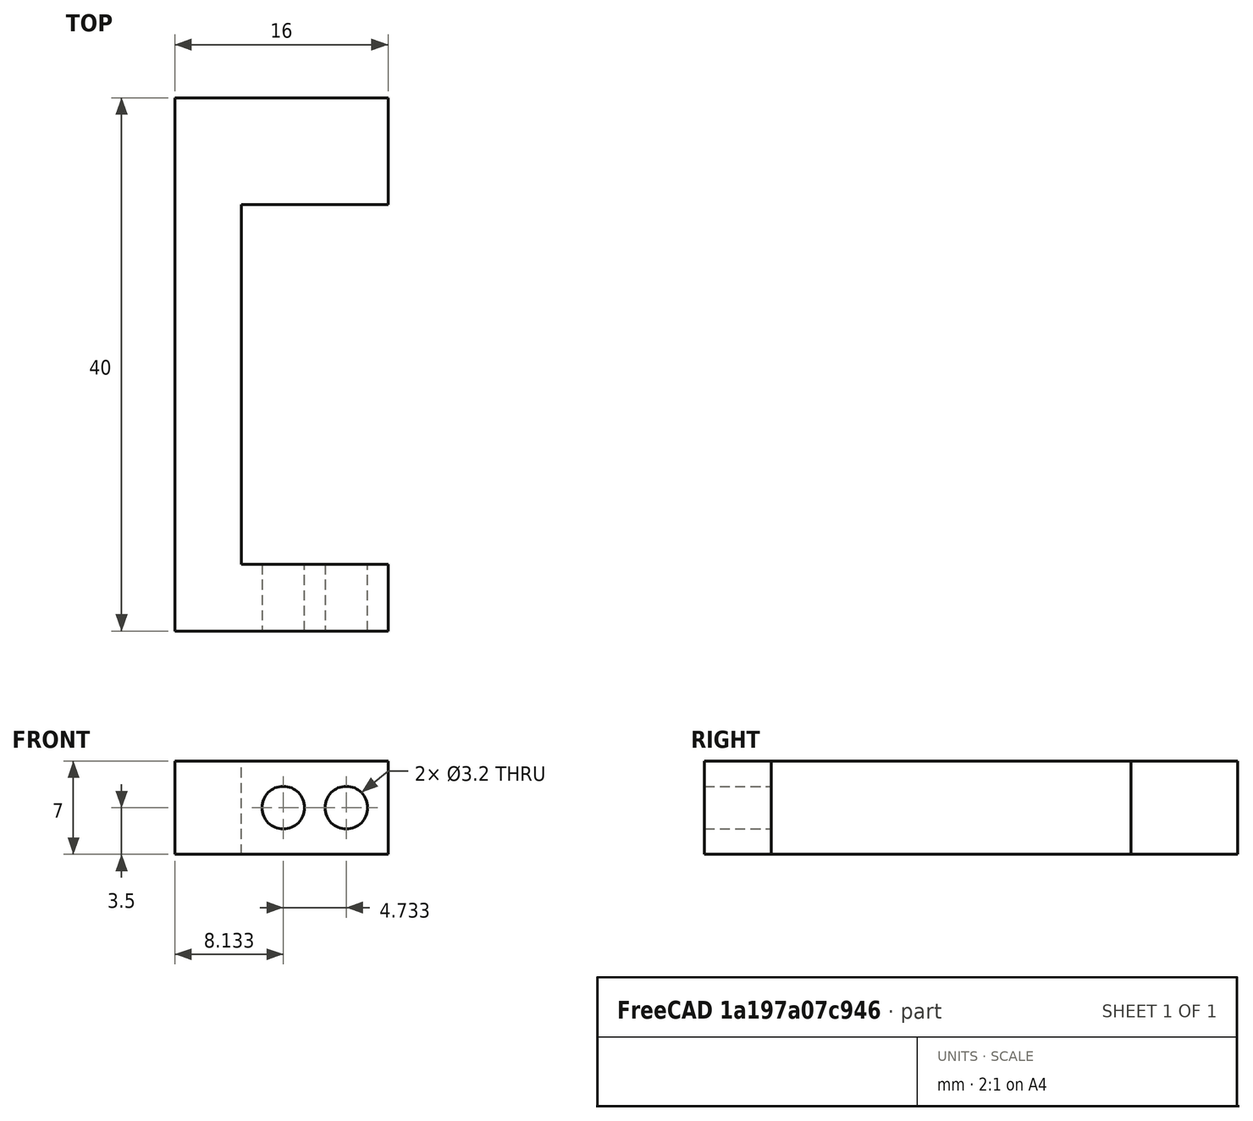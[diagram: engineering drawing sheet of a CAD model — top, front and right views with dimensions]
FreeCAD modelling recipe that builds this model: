
FCSTD DOCUMENT  (FreeCAD 0.18.4R)
Label: 10
License: All rights reserved
LicenseURL: http://en.wikipedia.org/wiki/All_rights_reserved
objects: Sketcher::SketchObject×2, PartDesign::Pad×1, PartDesign::Pocket×1, PartDesign::Body×1
note: 7 computed .brp shape members not serialized (recipe doc carries the construction recipe); baked Part::Feature solids carry a one-line shape summary decoded from their .brp

FEATURE [Sketcher::SketchObject] Sketch  label="Unnamed"
  constraints (23):
    c: Coincident(g-1,g0)
    c: PointOnObject(g0,g-2)
    c: Coincident(g0,g1)
    c: Horizontal(g1)
    c: Coincident(g1,g2)
    c: Vertical(g2)
    c: Coincident(g2,g3)
    c: Horizontal(g3)
    c: Coincident(g3,g4)
    c: Vertical(g4)
    c: Coincident(g4,g5)
    c: Horizontal(g5)
    c: Coincident(g5,g6)
    c: PointOnObject(g6,g-1)
    c: Vertical(g6)
    c: Coincident(g6,g7)
    c: Coincident(g7,g0)
    c: DistanceX(g4,g0) = 5
    c: DistanceX(g3,g3) = 16
    c: Distance(g2) = 8
    c: Distance(g4) = 40
    c: Distance(g6) = 5
    c: Vertical(g1,g6)
FEATURE [PartDesign::Pad] Pad  label="Unnamed"
  Length = 100
  Length2 = 100
  Type = 0
FEATURE [Sketcher::SketchObject] Sketch001  label="Unnamed"
FEATURE [PartDesign::Pocket] Pocket  label="Unnamed"
  Length = 100
  Length2 = 100
  Type = 0
FEATURE [PartDesign::Body] Body
  Group = -> [Sketch,Pad,Sketch001,Pocket]
  Origin = -> Origin
  Tip = -> Pocket
